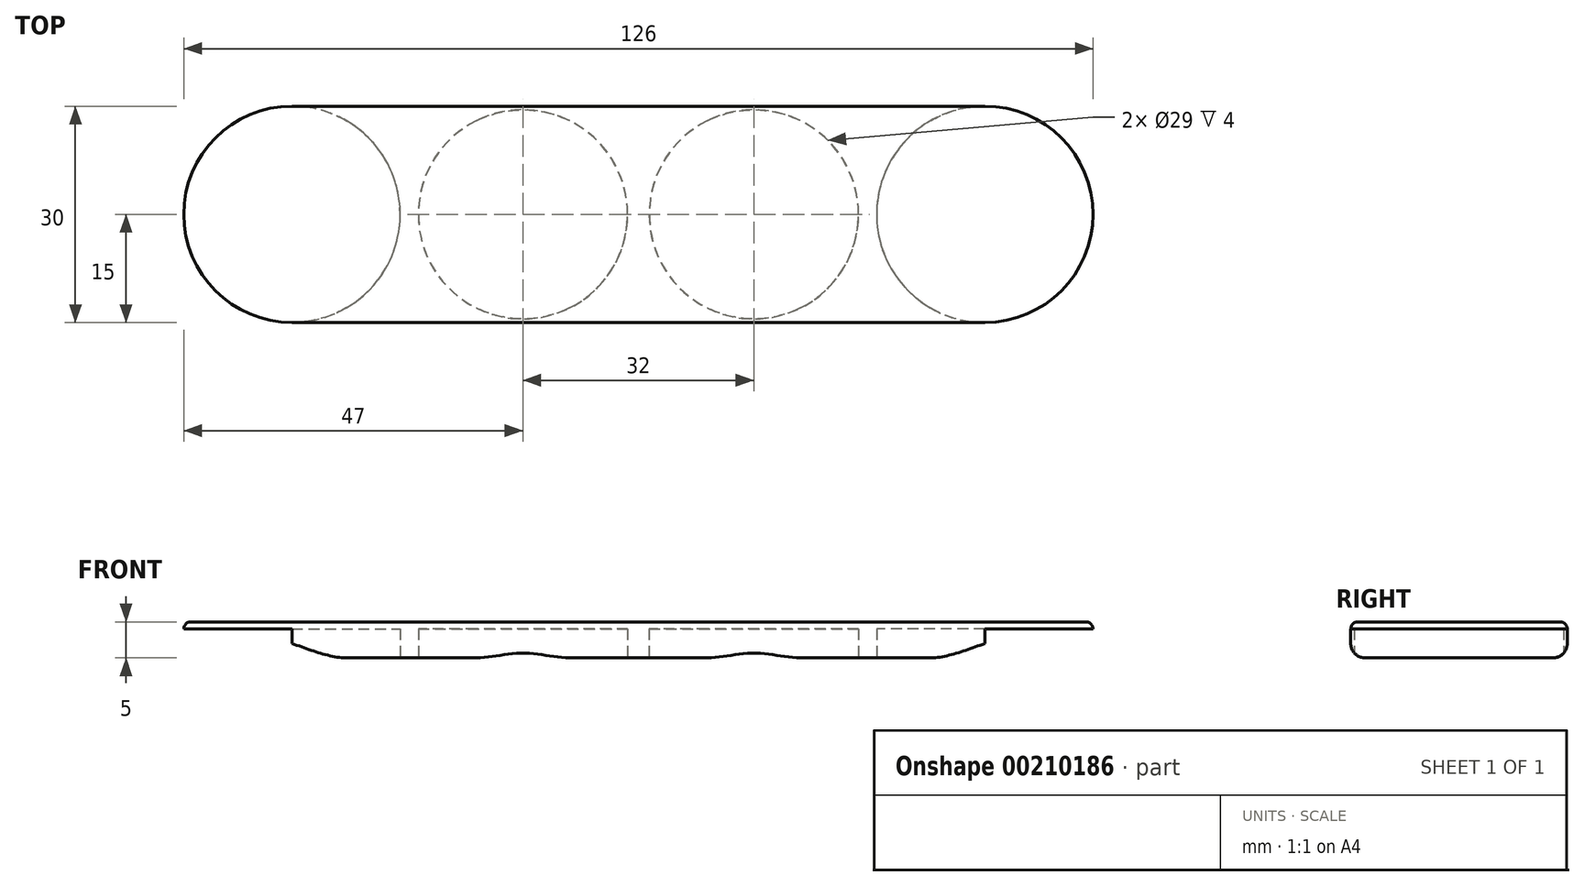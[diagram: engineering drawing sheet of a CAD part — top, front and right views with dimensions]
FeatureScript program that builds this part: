
annotation { "Feature Type Name" : "Feature", "Feature Type Description" : "" }
export const myFeature = defineFeature(function(context is Context, id is Id, definition is map)
    precondition{}
    {
        {
            var Q0;
            Q0=qCreatedBy(makeId("Top.planeOp"),FACE);
            var sketch = newSketch(context, id + "F0", { "sketchPlane" : qUnion([Q0])});
            skLineSegment(sketch, "E0", {"start": v(32, 0) * mm, "end": v(-73.56, 0) * mm, "construction": true});
            skLineSegment(sketch, "E1", {"start": v(0, 0) * mm, "end": v(0, 29.11) * mm, "construction": true});
            skLineSegment(sketch, "E2.0", {"start": v(-16, 0) * mm, "end": v(-16, 29.11) * mm, "construction": true});
            skLineSegment(sketch, "E3.0", {"start": v(-32, 0) * mm, "end": v(-32, 29.11) * mm, "construction": true});
            skLineSegment(sketch, "E4.0", {"start": v(-48, 0) * mm, "end": v(-48, 29.11) * mm, "construction": true});
            skLineSegment(sketch, "E5.0", {"start": v(-64, 0) * mm, "end": v(-64, 29.11) * mm, "construction": true});
            skCircle(sketch, "E6", {"center": v(-64, 0) * mm, "radius": 15 * mm});
            skLineSegment(sketch, "E7.0", {"start": v(16, 0) * mm, "end": v(16, 29.11) * mm, "construction": true});
            skLineSegment(sketch, "E8.0", {"start": v(32, 0) * mm, "end": v(32, 29.11) * mm, "construction": true});
            skCircle(sketch, "E9", {"center": v(-32, 0) * mm, "radius": 14.5 * mm});
            skCircle(sketch, "E10", {"center": v(0, 0) * mm, "radius": 14.5 * mm});
            skCircle(sketch, "E11", {"center": v(32, 0) * mm, "radius": 15 * mm});
            skLineSegment(sketch, "E12", {"start": v(-64, 15) * mm, "end": v(32, 15) * mm});
            skLineSegment(sketch, "E13.MirrorCS", {"start": v(-64, -15) * mm, "end": v(32, -15) * mm});
            skSolve(sketch);
        }
        {
            var Q0;
            {var subQ0=sQuery(id+"F0.wireOp",EDGE,"E11");var subQ1=makeQuery(id+"F0.imprint","INTERSECT",VERTEX,{"derivedFrom":[subQ0,sQuery(id+"F0.wireOp",EDGE,"E12")]});Q0=makeQuery(id+"F0.imprint","IMPRINT",FACE,{"disambiguationData":[TD([[makeQuery(id+"F0.imprint","IMPRINT",EDGE,{"disambiguationData":[TD([[subQ1,-1.0]])],"derivedFrom":subQ0}),1.0]])]});}
            var Q1;
            Q1=makeQuery(id+"F0.imprint","IMPRINT",FACE,{"disambiguationData":[TD([[makeQuery(id+"F0.imprint","IMPRINT",EDGE,{"derivedFrom":sQuery(id+"F0.wireOp",EDGE,"E9")}),-1.0]])]});
            var Q2;
            Q2=makeQuery(id+"F0.imprint","IMPRINT",FACE,{"disambiguationData":[TD([[makeQuery(id+"F0.imprint","IMPRINT",EDGE,{"derivedFrom":sQuery(id+"F0.wireOp",EDGE,"E10")}),1.0]])]});
            var Q3;
            Q3=makeQuery(id+"F0.imprint","IMPRINT",FACE,{"disambiguationData":[TD([[makeQuery(id+"F0.imprint","IMPRINT",EDGE,{"derivedFrom":sQuery(id+"F0.wireOp",EDGE,"E9")}),1.0]])]});
            var Q4;
            {var subQ0=sQuery(id+"F0.wireOp",EDGE,"E6");var subQ1=makeQuery(id+"F0.imprint","INTERSECT",VERTEX,{"derivedFrom":[subQ0,sQuery(id+"F0.wireOp",EDGE,"E12")]});Q4=makeQuery(id+"F0.imprint","IMPRINT",FACE,{"disambiguationData":[TD([[makeQuery(id+"F0.imprint","IMPRINT",EDGE,{"disambiguationData":[TD([[subQ1,-1.0]])],"derivedFrom":subQ0}),1.0]])]});}
            extrude(context, id + "F1", {"entities" : qUnion([Q0, Q1, Q2, Q3, Q4]), "depth" : 5 * mm});
        }
        {
            var Q0;
            {var subQ0=sQuery(id+"F0.wireOp",EDGE,"E11");var subQ1=makeQuery(id+"F0.imprint","INTERSECT",VERTEX,{"derivedFrom":[subQ0,sQuery(id+"F0.wireOp",EDGE,"E12")]});Q0=makeQuery(id+"F0.imprint","IMPRINT",FACE,{"disambiguationData":[TD([[makeQuery(id+"F0.imprint","IMPRINT",EDGE,{"disambiguationData":[TD([[subQ1,-1.0]])],"derivedFrom":subQ0}),1.0]])]});}
            var Q1;
            Q1=makeQuery(id+"F0.imprint","IMPRINT",FACE,{"disambiguationData":[TD([[makeQuery(id+"F0.imprint","IMPRINT",EDGE,{"derivedFrom":sQuery(id+"F0.wireOp",EDGE,"E10")}),1.0]])]});
            var Q2;
            Q2=makeQuery(id+"F0.imprint","IMPRINT",FACE,{"disambiguationData":[TD([[makeQuery(id+"F0.imprint","IMPRINT",EDGE,{"derivedFrom":sQuery(id+"F0.wireOp",EDGE,"E9")}),1.0]])]});
            var Q3;
            {var subQ0=sQuery(id+"F0.wireOp",EDGE,"E6");var subQ1=makeQuery(id+"F0.imprint","INTERSECT",VERTEX,{"derivedFrom":[subQ0,sQuery(id+"F0.wireOp",EDGE,"E12")]});Q3=makeQuery(id+"F0.imprint","IMPRINT",FACE,{"disambiguationData":[TD([[makeQuery(id+"F0.imprint","IMPRINT",EDGE,{"disambiguationData":[TD([[subQ1,-1.0]])],"derivedFrom":subQ0}),1.0]])]});}
            extrude(context, id + "F2", {"entities" : qUnion([Q0, Q1, Q2, Q3]), "operationType" : NewBodyOperationType.REMOVE, "depth" : 4 * mm});
        }
        {
            var Q0;
            Q0=makeQuery(id+"F1.opExtrude","CAP_EDGE",EDGE,{"disambiguationData":[OSD([sQuery(id+"F0.wireOp",EDGE,"E13.MirrorCS")])],"isStart":true});
            var Q1;
            Q1=makeQuery(id+"F1.opExtrude","CAP_EDGE",EDGE,{"disambiguationData":[OSD([sQuery(id+"F0.wireOp",EDGE,"E12")])],"isStart":true});
            fillet(context, id + "F3", {"entities" : qUnion([Q0, Q1]), "radius" : 2 * mm, "tangentPropagation" : true, "allowEdgeOverflow" : false});
        }
        {
            var Q0;
            Q0=makeQuery(id+"F1.opExtrude","CAP_FACE",FACE,{"disambiguationData":[OSD([sQuery(id+"F0.wireOp",EDGE,"E6"),sQuery(id+"F0.wireOp",EDGE,"E11"),sQuery(id+"F0.wireOp",EDGE,"E12"),sQuery(id+"F0.wireOp",EDGE,"E13.MirrorCS")])],"isStart":false});
            fillet(context, id + "F4", {"entities" : qUnion([Q0]), "radius" : 1 * mm, "tangentPropagation" : true, "allowEdgeOverflow" : false});
        }
    });
